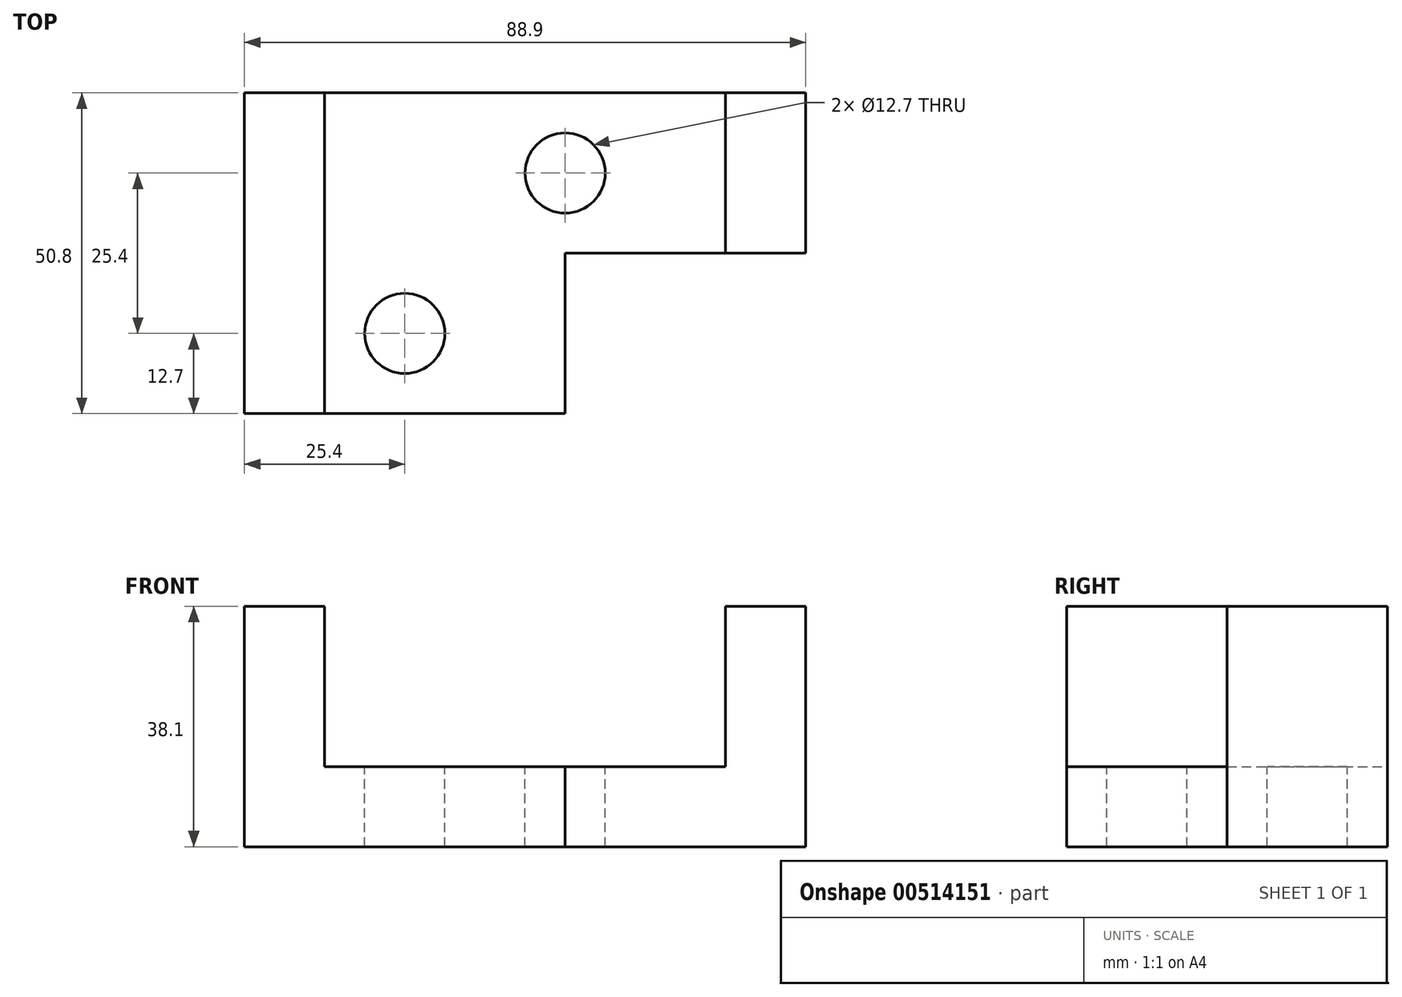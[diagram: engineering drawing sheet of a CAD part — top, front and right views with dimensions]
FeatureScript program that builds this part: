
annotation { "Feature Type Name" : "Feature", "Feature Type Description" : "" }
export const myFeature = defineFeature(function(context is Context, id is Id, definition is map)
    precondition{}
    {
        {
            var Q0;
            Q0=qCreatedBy(makeId("Front.planeOp"),FACE);
            var sketch = newSketch(context, id + "F0", { "sketchPlane" : qUnion([Q0])});
            skLineSegment(sketch, "E0.bottom", {"start": v(44.45, 19.05) * mm, "end": v(-44.45, 19.05) * mm});
            skLineSegment(sketch, "E0.top", {"start": v(44.45, -19.05) * mm, "end": v(-44.45, -19.05) * mm});
            skLineSegment(sketch, "E0.left", {"start": v(44.45, 19.05) * mm, "end": v(44.45, -19.05) * mm});
            skLineSegment(sketch, "E0.right", {"start": v(-44.45, 19.05) * mm, "end": v(-44.45, -19.05) * mm});
            skPoint(sketch, "E0.middle", {"position": v(0, 0) * mm});
            skSolve(sketch);
        }
        {
            var Q0;
            Q0=makeQuery(id+"F0.imprint","IMPRINT",FACE,{"disambiguationData":[TD([[makeQuery(id+"F0.imprint","IMPRINT",EDGE,{"derivedFrom":sQuery(id+"F0.wireOp",EDGE,"E0.bottom")}),1.0]])]});
            extrude(context, id + "F1", {"entities" : qUnion([Q0]), "depth" : 50.8 * mm});
        }
        {
            var Q0;
            Q0=makeQuery(id+"F1.opExtrude","SWEPT_FACE",FACE,{"disambiguationData":[OSD([sQuery(id+"F0.wireOp",EDGE,"E0.bottom")])]});
            var sketch = newSketch(context, id + "F2", { "sketchPlane" : qUnion([Q0])});
            skLineSegment(sketch, "E1", {"start": v(6.35, -50.8) * mm, "end": v(6.35, -25.4) * mm});
            skLineSegment(sketch, "E2", {"start": v(6.35, -25.4) * mm, "end": v(44.45, -25.4) * mm});
            skSolve(sketch);
        }
        {
            var Q0;
            {var subQ0=sQuery(id+"F2.wireOp",EDGE,"E1");Q0=makeQuery(id+"F2.imprint","IMPRINT",FACE,{"disambiguationData":[TD([[makeQuery(id+"F2.imprint","IMPRINT",EDGE,{"derivedFrom":subQ0}),-1.0]])]});}
            extrude(context, id + "F3", {"entities" : qUnion([Q0]), "operationType" : NewBodyOperationType.REMOVE, "oppositeDirection" : true, "depth" : 38.1 * mm});
        }
        {
            var Q0;
            Q0=makeQuery(id+"F1.opExtrude","CAP_FACE",FACE,{"disambiguationData":[OSD([sQuery(id+"F0.wireOp",EDGE,"E0.bottom"),sQuery(id+"F0.wireOp",EDGE,"E0.top"),sQuery(id+"F0.wireOp",EDGE,"E0.left"),sQuery(id+"F0.wireOp",EDGE,"E0.right")])],"isStart":true});
            var sketch = newSketch(context, id + "F4", { "sketchPlane" : qUnion([Q0])});
            skLineSegment(sketch, "E3.bottom", {"start": v(-31.75, 19.05) * mm, "end": v(31.75, 19.05) * mm});
            skLineSegment(sketch, "E3.top", {"start": v(-31.75, -6.35) * mm, "end": v(31.75, -6.35) * mm});
            skLineSegment(sketch, "E3.left", {"start": v(-31.75, 19.05) * mm, "end": v(-31.75, -6.35) * mm});
            skLineSegment(sketch, "E3.right", {"start": v(31.75, 19.05) * mm, "end": v(31.75, -6.35) * mm});
            skSolve(sketch);
        }
        {
            var Q0;
            Q0=makeQuery(id+"F4.imprint","IMPRINT",FACE,{"disambiguationData":[TD([[makeQuery(id+"F4.imprint","IMPRINT",EDGE,{"derivedFrom":sQuery(id+"F4.wireOp",EDGE,"E3.bottom")}),-1.0]])]});
            extrude(context, id + "F5", {"entities" : qUnion([Q0]), "operationType" : NewBodyOperationType.REMOVE, "oppositeDirection" : true, "depth" : 50.8 * mm});
        }
        {
            var Q0;
            Q0=makeQuery(id+"F5.boolean.opBoolean","COPY",FACE,{"derivedFrom":makeQuery(id+"F5.opExtrude","SWEPT_FACE",FACE,{"disambiguationData":[OSD([sQuery(id+"F4.wireOp",EDGE,"E3.top")])]})});
            var sketch = newSketch(context, id + "F6", { "sketchPlane" : qUnion([Q0])});
            skCircle(sketch, "E4", {"center": v(-19.05, -38.1) * mm, "radius": 6.35 * mm});
            skSolve(sketch);
        }
        {
            var Q0;
            Q0=makeQuery(id+"F6.imprint","IMPRINT",FACE,{"disambiguationData":[TD([[makeQuery(id+"F6.imprint","IMPRINT",EDGE,{"derivedFrom":sQuery(id+"F6.wireOp",EDGE,"E4")}),1.0]])]});
            extrude(context, id + "F7", {"entities" : qUnion([Q0]), "operationType" : NewBodyOperationType.REMOVE, "oppositeDirection" : true, "depth" : 12.7 * mm});
        }
        {
            var Q0;
            Q0=makeQuery(id+"F5.boolean.opBoolean","COPY",FACE,{"derivedFrom":makeQuery(id+"F5.opExtrude","SWEPT_FACE",FACE,{"disambiguationData":[OSD([sQuery(id+"F4.wireOp",EDGE,"E3.top")])]})});
            var sketch = newSketch(context, id + "F8", { "sketchPlane" : qUnion([Q0])});
            skCircle(sketch, "E5", {"center": v(6.35, -12.7) * mm, "radius": 6.35 * mm});
            skSolve(sketch);
        }
        {
            var Q0;
            Q0=makeQuery(id+"F8.imprint","IMPRINT",FACE,{"disambiguationData":[TD([[makeQuery(id+"F8.imprint","IMPRINT",EDGE,{"derivedFrom":sQuery(id+"F8.wireOp",EDGE,"E5")}),1.0]])]});
            extrude(context, id + "F9", {"entities" : qUnion([Q0]), "operationType" : NewBodyOperationType.REMOVE, "oppositeDirection" : true, "depth" : 12.7 * mm});
        }
    });
